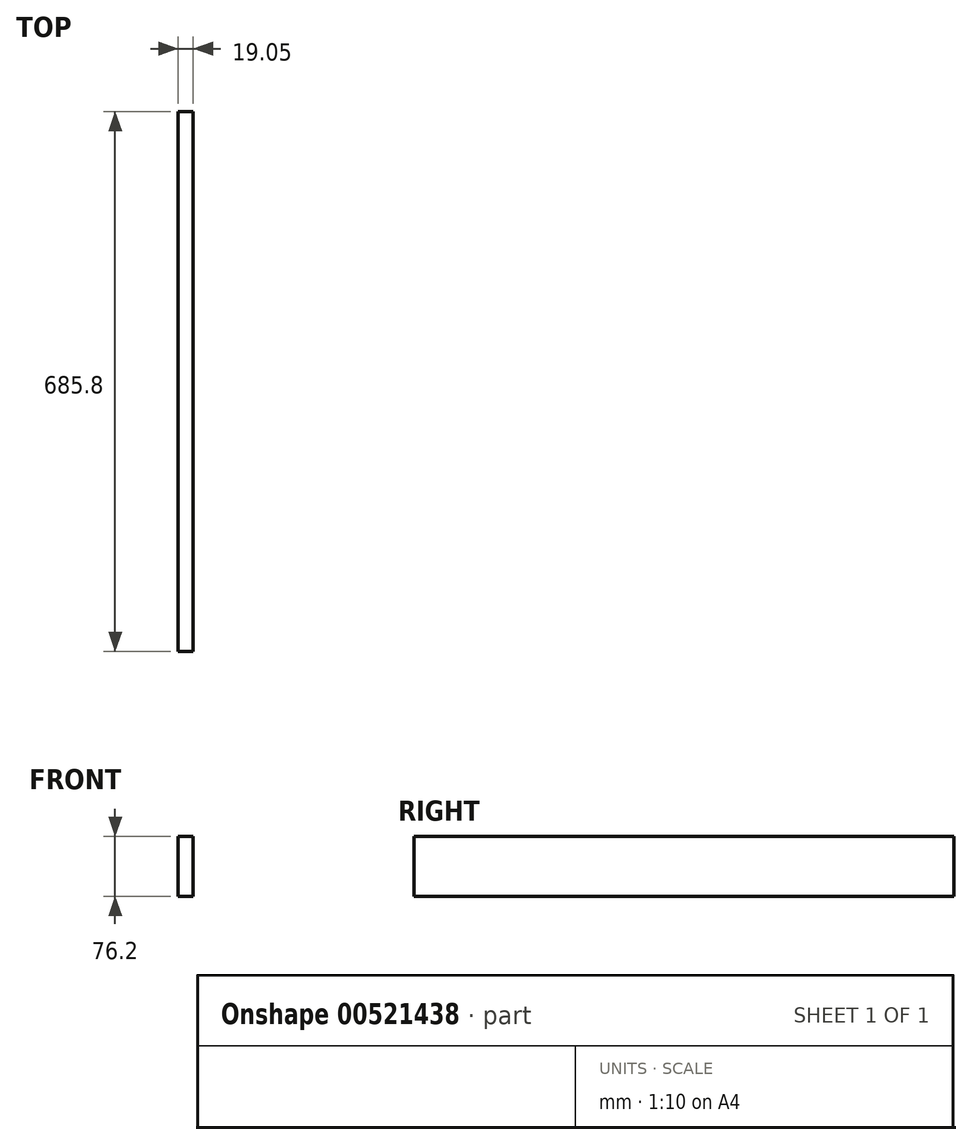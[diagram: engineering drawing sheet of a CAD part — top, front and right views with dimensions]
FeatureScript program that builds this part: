
annotation { "Feature Type Name" : "Feature", "Feature Type Description" : "" }
export const myFeature = defineFeature(function(context is Context, id is Id, definition is map)
    precondition{}
    {
        {
            var Q0;
            Q0=qCreatedBy(makeId("Top.planeOp"),FACE);
            var sketch = newSketch(context, id + "F0", { "sketchPlane" : qUnion([Q0])});
            skLineSegment(sketch, "E0.bottom", {"start": v(0, 282.99) * mm, "end": v(19.05, 282.99) * mm});
            skLineSegment(sketch, "E0.top", {"start": v(0, -402.81) * mm, "end": v(19.05, -402.81) * mm});
            skLineSegment(sketch, "E0.left", {"start": v(0, 282.99) * mm, "end": v(0, -402.81) * mm});
            skLineSegment(sketch, "E0.right", {"start": v(19.05, 282.99) * mm, "end": v(19.05, -402.81) * mm});
            skSolve(sketch);
        }
        {
            var Q0;
            Q0=makeQuery(id+"F0.imprint","IMPRINT",FACE,{"disambiguationData":[TD([[makeQuery(id+"F0.imprint","IMPRINT",EDGE,{"derivedFrom":sQuery(id+"F0.wireOp",EDGE,"E0.bottom")}),-1.0]])]});
            extrude(context, id + "F1", {"entities" : qUnion([Q0]), "depth" : 76.2 * mm, "offsetDistance" : 25.4 * mm});
        }
    });
